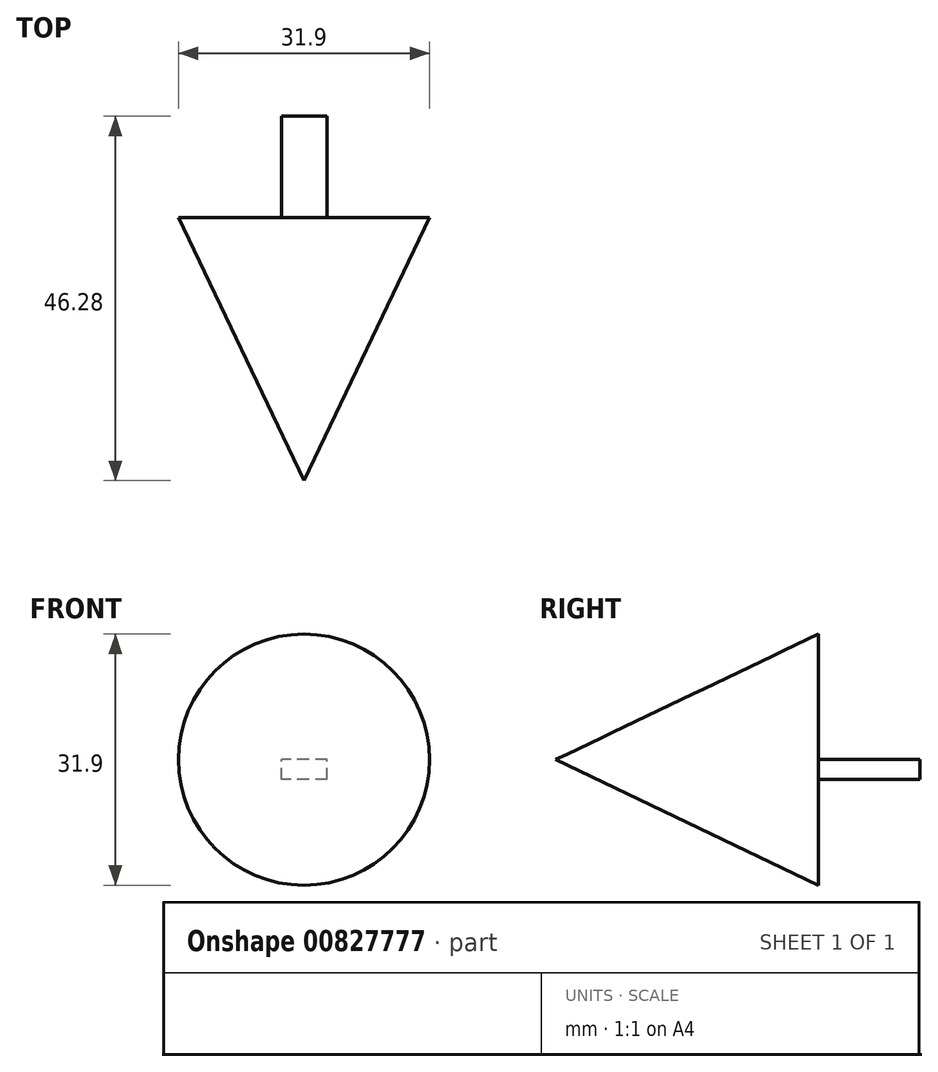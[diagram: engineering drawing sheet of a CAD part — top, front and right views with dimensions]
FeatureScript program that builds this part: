
annotation { "Feature Type Name" : "Feature", "Feature Type Description" : "" }
export const myFeature = defineFeature(function(context is Context, id is Id, definition is map)
    precondition{}
    {
        {
            var Q0;
            Q0=qCreatedBy(makeId("Right.planeOp"),FACE);
            var sketch = newSketch(context, id + "F0", { "sketchPlane" : qUnion([Q0])});
            skLineSegment(sketch, "E0", {"start": v(0, 0) * mm, "end": v(-33.4, 0) * mm});
            skLineSegment(sketch, "E1", {"start": v(-33.4, 0) * mm, "end": v(0, 15.95) * mm});
            skLineSegment(sketch, "E2", {"start": v(0, 15.95) * mm, "end": v(0, 0) * mm});
            skSolve(sketch);
        }
        {
            var Q0;
            Q0=qCreatedBy(makeId("Right.planeOp"),FACE);
            var sketch = newSketch(context, id + "F1", { "sketchPlane" : qUnion([Q0])});
            skLineSegment(sketch, "E3", {"start": v(-50.42, 0) * mm, "end": v(-38.18, 0) * mm});
            skSolve(sketch);
        }
        {
            var Q0;
            Q0=makeQuery(id+"F0.imprint","IMPRINT",FACE,{"disambiguationData":[TD([[makeQuery(id+"F0.imprint","IMPRINT",EDGE,{"derivedFrom":sQuery(id+"F0.wireOp",EDGE,"E0")}),-1.0]])]});
            var Q1;
            Q1=sQuery(id+"F1.wireOp",EDGE,"E3");
            revolve(context, id + "F2", {"surfaceOperationType" : NewSurfaceOperationType.NEW, "entities" : qUnion([Q0]), "axis" : qUnion([Q1]), "revolveType" : RevolveType.FULL});
        }
        {
            var Q0;
            Q0=qCreatedBy(makeId("Top.planeOp"),FACE);
            var sketch = newSketch(context, id + "F3", { "sketchPlane" : qUnion([Q0])});
            skLineSegment(sketch, "E4.bottom", {"start": v(2.95, 12.87) * mm, "end": v(-2.86, 12.87) * mm});
            skLineSegment(sketch, "E4.top", {"start": v(2.95, 0) * mm, "end": v(-2.86, 0) * mm});
            skLineSegment(sketch, "E4.left", {"start": v(2.95, 12.87) * mm, "end": v(2.95, 0) * mm});
            skLineSegment(sketch, "E4.right", {"start": v(-2.86, 12.87) * mm, "end": v(-2.86, 0) * mm});
            skSolve(sketch);
        }
        {
            var Q0;
            Q0=makeQuery(id+"F3.imprint","IMPRINT",FACE,{"disambiguationData":[TD([[makeQuery(id+"F3.imprint","IMPRINT",EDGE,{"derivedFrom":sQuery(id+"F3.wireOp",EDGE,"E4.bottom")}),1.0]])]});
            extrude(context, id + "F4", {"entities" : qUnion([Q0]), "operationType" : NewBodyOperationType.ADD, "oppositeDirection" : true, "depth" : 2.54 * mm, "offsetDistance" : 25.4 * mm});
        }
    });
